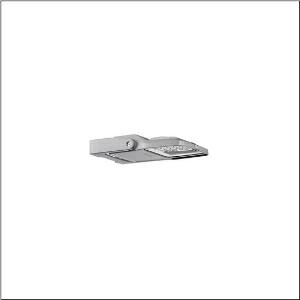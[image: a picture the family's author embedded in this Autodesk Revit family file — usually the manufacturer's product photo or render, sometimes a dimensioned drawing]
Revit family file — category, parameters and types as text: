
# Revit family: floodlight_fl_21_iq_micro___pl64_5xa7762a2e2a_90eb
name_source: partatom
category: Lighting Fixtures
units: mm (PartAtom-declared; Revit-internal decimal feet)

## family parameters
Cut with Voids When Loaded = No
Host = Face
Light Source = No
Part Type = Normal
Room Calculation Point = No
Round Connector Dimension = Use Diameter
Shared = No

## types (1)
- --- (1 x LED, 2870 lm, 23.1 W, 3000K)
    Apparent Load = 23 VA
    CIE Flux Codes = 28 80 98 100 100
    Color Rendering = 70
    Color Temperature = 3000K
    Default Elevation = 1800 mm
    Description = Floodlight FL 21 iQ micro, floodlight, primary light control with lens, of PMMA, primary optical cover: protective disc, of toughened safety glass, transparent, light distribution: PL64, light emission: direct distribution, installation type: surface-mounted, LED, High Power LED, rated luminous flux: 2.870lm, luminous efficacy: 124lm/W, light colour: 730, colour temperature: 3000K, control: Auto-Match, Temp-Guard, Night-Set, Smart-Wire, Desk-Remote (wireless, voltage-free reading and setting of iQ features in the workshop via application-optimized NFC function/RFID function), optimised constant luminous flux control (CLO 2.0), Street-Remote, with terminal, 6-pole, mains connection: 220..240V, AC, 50/60Hz, start of lifetime: 23W, end of service life: 24W, reduction: 11W, luminaire housing, of diecast aluminium, powder-coated, Siteco® metallic grey (DB 702S), corrosivity category C5 mid according to DIN EN ISO 12944, sealing non-destructively replaceable, design bracket, of diecast aluminium, powder-coated, Siteco® metallic grey (DB 702S), protection rating (complete): IP66, insulation class (complete): insulation class II (safety insulation), certification: CE, ENEC, VDE, protection symbol: D, impact resistance: IK07, permissible operating ambient temperature: -40..+40°C, permissible operating ambient temperature for outdoor applications: -40..+50°C, standard: DIN EN 12944, LABS conformity tested according to VDMA 24364:2018-05, packaging unit: 1 piece

Light Distribution: PL64
    Height = 65 mm
    Lamp = 1 x LED
    Lamp Light Flux = 2870 lm
    Lamp Power = 23.1 W
    Lamp count = 1
    Length = 312 mm
    Luminous efficacy = 124 lm/W
    Manufacturer = Siteco
    ModVariant = No
    Model = 5XA7762A2E2A
    Mounting Place = Wall
    Mounting Type = Surface mounted
    Number of Poles = 1
    OnlyDefault = Yes
    Power Factor = 1
    Product Name = Floodlight FL 21 iQ micro | PL64
    Product group = floodlight | wall mounted
    ProductGroupID = 2001
    Protection Class = Protection class II
    Protection Degree = IP 66
    RLX_Detail_Level = 1
    RLX_Emergency_Light_Flux = 0 lm
    RLX_Emergency_Type = 0
    RLX_Emergency_Type_DB = No
    RlxData = <blob elided: 97317 chars, md5=37a56226>
    Socket = socket
    Standby Power = 0 W
    System Light Flux = 2870 lm
    System Power = 23 W
    Type Comments = factory setting: luminous flux: 100 % | dim-lin: 254 | 455 mA
    Type Image = l_1006878.jpg
    URL = http://relux.com
    VarID = @adj_113719
    Voltage = 0 V
    Weight = 0.00 kg
    Width = 230 mm

## geometry (parser evidence)
native form markers: Blend x4, Sweep x13
no freeform markers — native parametric forms only
